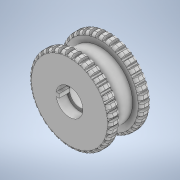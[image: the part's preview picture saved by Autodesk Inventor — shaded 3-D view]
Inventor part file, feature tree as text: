
AUTODESK INVENTOR PART (.ipt)
format: ipt  version: 2021 (Build 250183000, 183)  size: 1,505,280 bytes
history: native  units: mm
features: extrude x8, fillet x5, sketch x4, plane x2, pattern_circular x2
ambient origin geometry x8: Origin, YZ Plane, XZ Plane, XY Plane, X Axis, Y Axis, Z Axis, Center Point
bodies: Solid1 (feature_tree)
feature tree (21):
  sketch  "Sketch1"  dims[d0=80.0mm d1=0.0mm]
  extrude  "Extrusion2"  TaperAngle=0.0deg  [1 undecoded]
  plane  "Work Plane2"
  plane  "Work Plane1"
  sketch  "Sketch4"  dims[d2=0.0mm d3=0.0mm]
  extrude  "Extrusion3"  TaperAngle=0.0deg  [1 undecoded]
  extrude  "Extrusion4"  Depth=74.0mm
  extrude  "Extrusion5"  Depth=0.5mm
  extrude  "Extrusion6"  Depth=0.5mm
  fillet  "Fillet4"  Radius=36.936003mm
  fillet  "Fillet5"  Radius=2.175251mm
  fillet  "Fillet6"  Radius=2.061732mm
  pattern_circular  "Circular Pattern4"  [2 undecoded]
  sketch  "Sketch5"  dims[d4=0.0mm d5=74.0mm]
  extrude  "Extrusion7"  Depth=10.0mm TaperAngle=0.0deg
  extrude  "Extrusion8"  Depth=0.5mm
  fillet  "Fillet9"  Radius=10.0mm
  fillet  "Fillet10"  Radius=63.0mm
  pattern_circular  "Circular Pattern5"  Count=2  [1 undecoded]
  extrude  "Extrusion9"  TaperAngle=0.0deg  [1 undecoded]
  sketch  "Sketch6"  dims[d6=75.6mm d7=2.0625mm d9=14.3117mm d10=36.936003mm d11=2.175251mm d12=2.061732mm d13=11.285177mm d16=10.0mm d17=0.0mm d44=20.0mm d45=10.0mm d46=0.0mm d47=63.0mm d48=20.0mm d49=0.0mm d50=0.0mm d51=0.0mm d52=25.0mm d53=30.0mm d54=0.0mm d55=10.0mm d56=0.0mm d57=3.0mm d58=3.0mm d59=0.5mm d60=360.0mm d61=360.0deg d63=80.0mm d64=0.0mm d65=0.0mm d66=0.0mm d67=0.0mm d68=74.0mm d69=75.6mm d70=2.0625mm d71=14.3117mm d72=36.936003mm d73=2.175251mm d74=2.061732mm d75=11.285177mm d76=10.0mm d77=0.0mm d80=10.0mm d81=0.0mm d82=3.0mm d83=0.5mm d84=360.0mm d85=360.0deg d88=10.0mm d89=0.0mm d14=0.5mm d15=0.872665mm d24=0.5mm d25=0.872665mm d26=0.5mm d27=0.872665mm]
note: 6 required parameter values undecoded (feature->parameter linkage not recoverable at this tier; creation-order binding heuristic only, values carry confidence <= 0.55)
